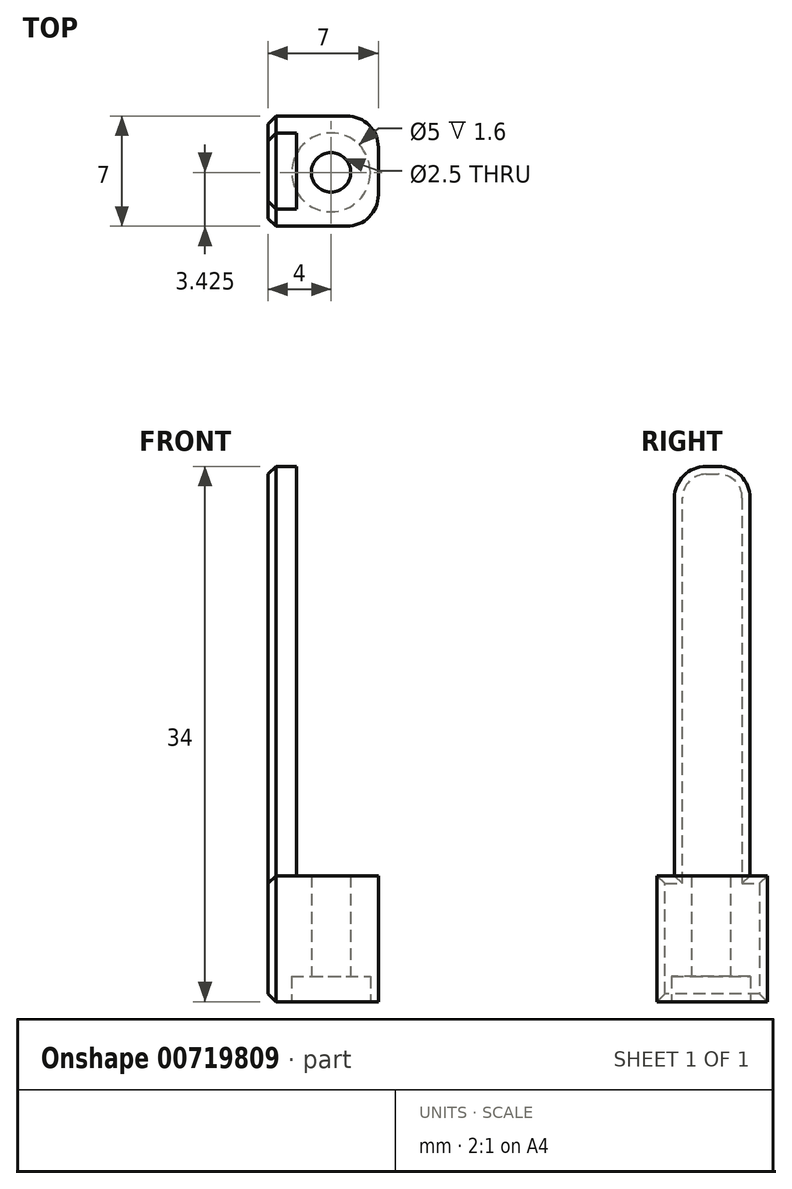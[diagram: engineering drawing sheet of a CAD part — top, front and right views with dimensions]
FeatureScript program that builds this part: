
annotation { "Feature Type Name" : "Feature", "Feature Type Description" : "" }
export const myFeature = defineFeature(function(context is Context, id is Id, definition is map)
    precondition{}
    {
        {
            var Q0;
            Q0=qCreatedBy(makeId("Top.planeOp"),FACE);
            var sketch = newSketch(context, id + "F0", { "sketchPlane" : qUnion([Q0])});
            skLineSegment(sketch, "E0.bottom", {"start": v(-4, 21.81) * mm, "end": v(1, 21.81) * mm});
            skLineSegment(sketch, "E0.top", {"start": v(-4, 14.81) * mm, "end": v(1, 14.81) * mm});
            skLineSegment(sketch, "E0.left", {"start": v(3, 16.81) * mm, "end": v(3, 19.81) * mm});
            skLineSegment(sketch, "E0.right", {"start": v(-4, 14.81) * mm, "end": v(-4, 21.81) * mm});
            skPoint(sketch, "E1.visualSharp", {"position": v(3, 21.81) * mm});
            skArc(sketch, "E1.filletArc", {"start": v(3, 19.81) * mm, "mid": v(2.41, 21.23) * mm, "end": v(1, 21.81) * mm});
            skPoint(sketch, "E2.visualSharp", {"position": v(3, 14.81) * mm});
            skArc(sketch, "E2.filletArc", {"start": v(1, 14.81) * mm, "mid": v(2.41, 15.4) * mm, "end": v(3, 16.81) * mm});
            skSolve(sketch);
        }
        {
            var Q0;
            Q0=makeQuery(id+"F0.imprint","IMPRINT",FACE,{"disambiguationData":[TD([[makeQuery(id+"F0.imprint","IMPRINT",EDGE,{"derivedFrom":sQuery(id+"F0.wireOp",EDGE,"E0.bottom")}),-1.0]])]});
            var Q1;
            Q1=makeQuery(id+"F0.imprint","IMPRINT",FACE,{"disambiguationData":[TD([[makeQuery(id+"F0.imprint","IMPRINT",EDGE,{"derivedFrom":sQuery(id+"F0.wireOp",EDGE,"OGHk75Aa-BJnh-hkSo-yNRI-ETdDBhqNUhSb")}),1.0]])]});
            var Q2;
            Q2=makeQuery(id+"F0.imprint","IMPRINT",FACE,{"disambiguationData":[TD([[makeQuery(id+"F0.imprint","IMPRINT",EDGE,{"derivedFrom":sQuery(id+"F0.wireOp",EDGE,"Jd6CkG7M-QaOW-uCvP-q8XN-jmcHcbD0AcgO")}),1.0]])]});
            extrude(context, id + "F1", {"entities" : qUnion([Q0, Q1, Q2]), "depth" : 8 * mm, "offsetDistance" : 25 * mm});
        }
        {
            var Q0;
            Q0=makeQuery(id+"F1.opExtrude","CAP_FACE",FACE,{"disambiguationData":[OSD([sQuery(id+"F0.wireOp",EDGE,"E0.bottom"),sQuery(id+"F0.wireOp",EDGE,"E0.top"),sQuery(id+"F0.wireOp",EDGE,"E0.left"),sQuery(id+"F0.wireOp",EDGE,"E0.right"),sQuery(id+"F0.wireOp",EDGE,"E1.filletArc"),sQuery(id+"F0.wireOp",EDGE,"E2.filletArc")])],"isStart":true});
            var sketch = newSketch(context, id + "F2", { "sketchPlane" : qUnion([Q0])});
            skCircle(sketch, "E3", {"center": v(0, -18.23) * mm, "radius": 2.5 * mm});
            skSolve(sketch);
        }
        {
            var Q0;
            Q0=qSketchRegion(id+"F2",true);
            extrude(context, id + "F3", {"entities" : qUnion([Q0]), "operationType" : NewBodyOperationType.REMOVE, "oppositeDirection" : true, "depth" : 1.6 * mm, "offsetDistance" : 25 * mm});
        }
        {
            var Q0;
            Q0=makeQuery(id+"F3.boolean.opBoolean","COPY",FACE,{"derivedFrom":makeQuery(id+"F3.opExtrude","CAP_FACE",FACE,{"disambiguationData":[OSD([sQuery(id+"F2.wireOp",EDGE,"E3")])],"isStart":false})});
            var sketch = newSketch(context, id + "F4", { "sketchPlane" : qUnion([Q0])});
            skCircle(sketch, "E4", {"center": v(0, -18.23) * mm, "radius": 1.25 * mm});
            skSolve(sketch);
        }
        {
            var Q0;
            Q0=qSketchRegion(id+"F4",true);
            extrude(context, id + "F5", {"entities" : qUnion([Q0]), "operationType" : NewBodyOperationType.REMOVE, "oppositeDirection" : true, "depth" : 10 * mm, "offsetDistance" : 25 * mm});
        }
        {
            var Q0;
            Q0=makeQuery(id+"F1.opExtrude","CAP_FACE",FACE,{"disambiguationData":[OSD([sQuery(id+"F0.wireOp",EDGE,"E0.bottom"),sQuery(id+"F0.wireOp",EDGE,"E0.top"),sQuery(id+"F0.wireOp",EDGE,"E0.left"),sQuery(id+"F0.wireOp",EDGE,"E0.right"),sQuery(id+"F0.wireOp",EDGE,"E1.filletArc"),sQuery(id+"F0.wireOp",EDGE,"E2.filletArc")])],"isStart":false});
            var sketch = newSketch(context, id + "F6", { "sketchPlane" : qUnion([Q0])});
            skLineSegment(sketch, "E5.bottom", {"start": v(-4, 20.71) * mm, "end": v(-2, 20.71) * mm});
            skLineSegment(sketch, "E5.top", {"start": v(-4, 15.91) * mm, "end": v(-2, 15.91) * mm});
            skLineSegment(sketch, "E5.left", {"start": v(-4, 20.71) * mm, "end": v(-4, 15.91) * mm});
            skLineSegment(sketch, "E5.right", {"start": v(-2, 20.71) * mm, "end": v(-2, 15.91) * mm});
            skSolve(sketch);
        }
        {
            var Q0;
            Q0=qSketchRegion(id+"F6",true);
            extrude(context, id + "F7", {"entities" : qUnion([Q0]), "operationType" : NewBodyOperationType.ADD, "depth" : 26 * mm, "offsetDistance" : 25 * mm});
        }
        {
            var Q0;
            Q0=makeQuery(id+"F7.opExtrude","CAP_EDGE",EDGE,{"disambiguationData":[OSD([sQuery(id+"F6.wireOp",EDGE,"E5.bottom")])],"isStart":false});
            var Q1;
            Q1=makeQuery(id+"F7.opExtrude","CAP_EDGE",EDGE,{"disambiguationData":[OSD([sQuery(id+"F6.wireOp",EDGE,"E5.top")])],"isStart":false});
            fillet(context, id + "F8", {"entities" : qUnion([Q0, Q1]), "radius" : 2 * mm, "tangentPropagation" : true, "allowEdgeOverflow" : false});
        }
        {
            var Q0;
            Q0=makeQuery(id+"F7.opExtrude","SWEPT_FACE",FACE,{"disambiguationData":[OSD([sQuery(id+"F6.wireOp",EDGE,"E5.right")])]});
            extrude(context, id + "F9", {"entities" : qUnion([Q0]), "operationType" : NewBodyOperationType.REMOVE, "oppositeDirection" : true, "depth" : 0.2 * mm, "offsetDistance" : 25 * mm});
        }
        {
            var Q0;
            Q0=makeQuery(id+"F7.boolean.opBoolean","MERGE",FACE,{"derivedFrom":[makeQuery(id+"F1.opExtrude","SWEPT_FACE",FACE,{"disambiguationData":[OSD([sQuery(id+"F0.wireOp",EDGE,"E0.right")])]}),makeQuery(id+"F7.opExtrude","SWEPT_FACE",FACE,{"disambiguationData":[OSD([sQuery(id+"F6.wireOp",EDGE,"E5.left")])]})]});
            extrude(context, id + "F10", {"entities" : qUnion([Q0]), "operationType" : NewBodyOperationType.ADD, "oppositeDirection" : true, "depth" : 0.4 * mm, "offsetDistance" : 25 * mm});
        }
        {
            var Q0;
            Q0=makeQuery(id+"F7.boolean.opBoolean","MERGE",FACE,{"derivedFrom":[makeQuery(id+"F1.opExtrude","SWEPT_FACE",FACE,{"disambiguationData":[OSD([sQuery(id+"F0.wireOp",EDGE,"E0.right")])]}),makeQuery(id+"F7.opExtrude","SWEPT_FACE",FACE,{"disambiguationData":[OSD([sQuery(id+"F6.wireOp",EDGE,"E5.left")])]})]});
            chamfer(context, id + "F11", {"entities" : qUnion([Q0]), "width" : 0.5 * mm, "tangentPropagation" : true});
        }
    });
